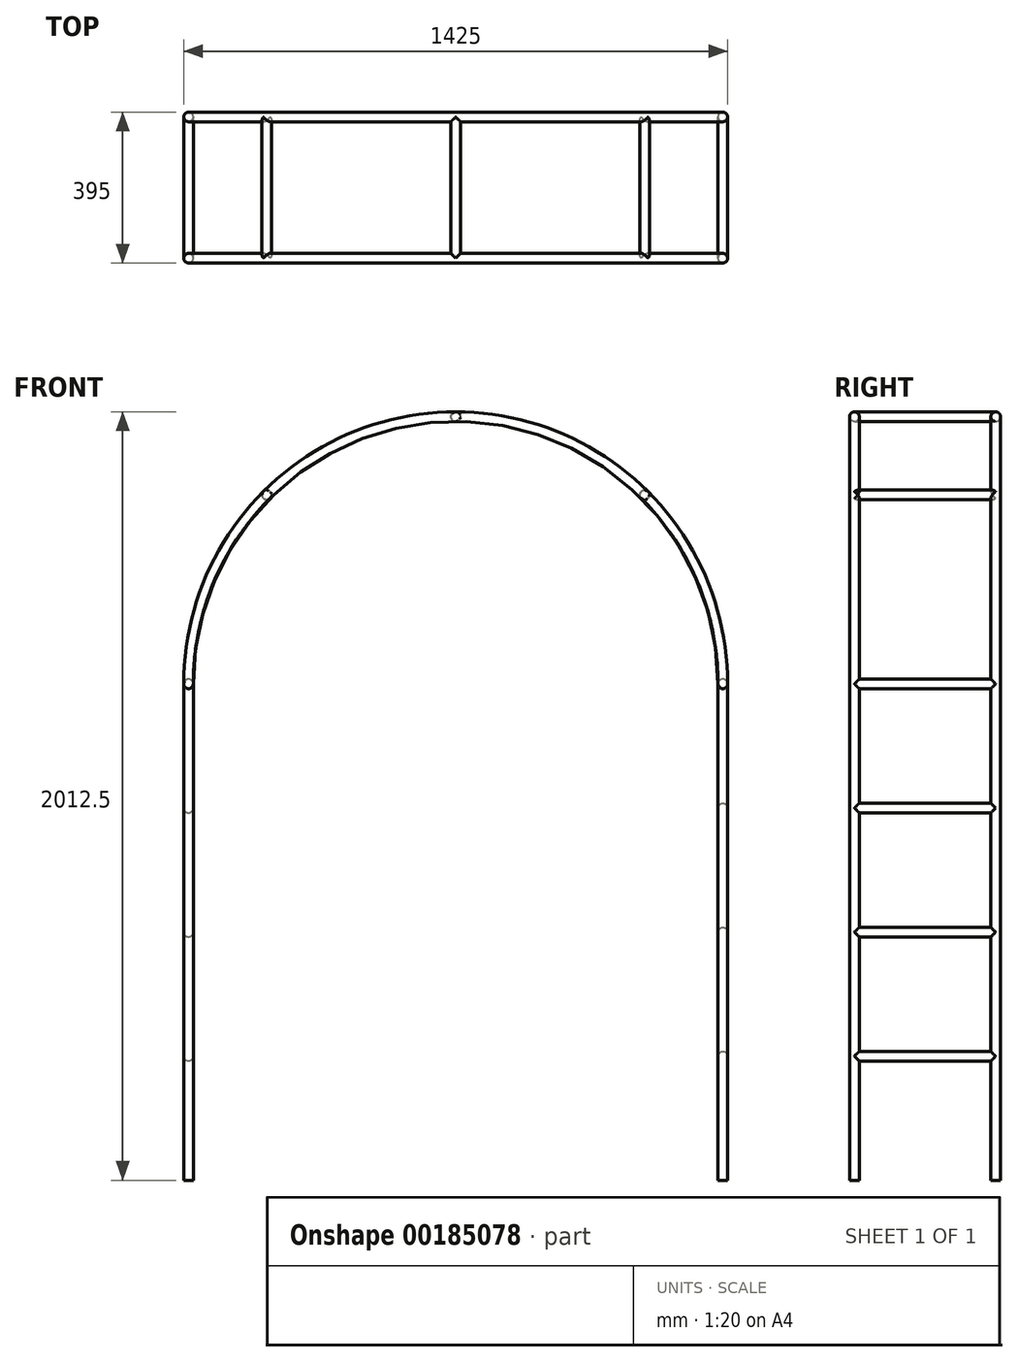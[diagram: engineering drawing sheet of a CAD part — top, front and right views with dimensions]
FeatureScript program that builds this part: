
annotation { "Feature Type Name" : "Feature", "Feature Type Description" : "" }
export const myFeature = defineFeature(function(context is Context, id is Id, definition is map)
    precondition{}
    {
        {
            var Q0;
            Q0=qCreatedBy(makeId("Top.planeOp"),FACE);
            var sketch = newSketch(context, id + "F0", { "sketchPlane" : qUnion([Q0])});
            skCircle(sketch, "E0", {"center": v(-700, 0) * mm, "radius": 12.5 * mm});
            skLineSegment(sketch, "E1", {"start": v(0, 35.36) * mm, "end": v(0, -370) * mm, "construction": true});
            skCircle(sketch, "E2", {"center": v(-700, -370) * mm, "radius": 12.5 * mm});
            skSolve(sketch);
        }
        {
            var Q0;
            Q0=makeQuery(id+"F0.imprint","IMPRINT",FACE,{"disambiguationData":[TD([[makeQuery(id+"F0.imprint","IMPRINT",EDGE,{"derivedFrom":sQuery(id+"F0.wireOp",EDGE,"E0")}),1.0]])]});
            var Q1;
            Q1=makeQuery(id+"F0.imprint","IMPRINT",FACE,{"disambiguationData":[TD([[makeQuery(id+"F0.imprint","IMPRINT",EDGE,{"derivedFrom":sQuery(id+"F0.wireOp",EDGE,"E2")}),1.0]])]});
            var Q2;
            Q2=sQuery(id+"F0.wireOp",EDGE,"E1");
            revolve(context, id + "F1", {"entities" : qUnion([Q0, Q1]), "axis" : qUnion([Q2]), "revolveType" : RevolveType.ONE_DIRECTION, "oppositeDirection" : true, "angle" : 180 * degree});
        }
        {
            var Q0;
            Q0=makeQuery(id+"F1.opRevolve","CAP_FACE",FACE,{"disambiguationData":[OSD([sQuery(id+"F0.wireOp",EDGE,"E0")])],"isStart":true});
            var Q1;
            Q1=makeQuery(id+"F1.opRevolve","CAP_FACE",FACE,{"disambiguationData":[OSD([sQuery(id+"F0.wireOp",EDGE,"E0")])],"isStart":false});
            extrude(context, id + "F2", {"entities" : qUnion([Q0, Q1]), "operationType" : NewBodyOperationType.ADD, "depth" : 1300 * mm});
        }
        {
            var Q0;
            Q0=makeQuery(id+"F1.opRevolve","CAP_FACE",FACE,{"disambiguationData":[OSD([sQuery(id+"F0.wireOp",EDGE,"E2")])],"isStart":true});
            var Q1;
            Q1=makeQuery(id+"F1.opRevolve","CAP_FACE",FACE,{"disambiguationData":[OSD([sQuery(id+"F0.wireOp",EDGE,"E2")])],"isStart":false});
            extrude(context, id + "F3", {"entities" : qUnion([Q0, Q1]), "operationType" : NewBodyOperationType.ADD, "depth" : 1300 * mm});
        }
        {
            var Q0;
            Q0=qCreatedBy(makeId("Front.planeOp"),FACE);
            var sketch = newSketch(context, id + "F4", { "sketchPlane" : qUnion([Q0])});
            skCircle(sketch, "E3", {"center": v(700, -975) * mm, "radius": 12.5 * mm});
            skCircle(sketch, "E4", {"center": v(700, -650) * mm, "radius": 12.5 * mm});
            skCircle(sketch, "E5", {"center": v(700, -325) * mm, "radius": 12.5 * mm});
            skCircle(sketch, "E6", {"center": v(700, 0) * mm, "radius": 12.5 * mm});
            skLineSegment(sketch, "E7", {"start": v(0, 0) * mm, "end": v(0, -1386.76) * mm, "construction": true});
            skCircle(sketch, "E8.MirrorC", {"center": v(-700, 0) * mm, "radius": 12.5 * mm});
            skCircle(sketch, "E9.MirrorC", {"center": v(-700, -325) * mm, "radius": 12.5 * mm});
            skCircle(sketch, "E10.MirrorC", {"center": v(-700, -650) * mm, "radius": 12.5 * mm});
            skCircle(sketch, "E11.MirrorC", {"center": v(-700, -975) * mm, "radius": 12.5 * mm});
            skPoint(sketch, "E12", {"position": v(0, 687.5) * mm});
            skPoint(sketch, "E13", {"position": v(0, 712.5) * mm});
            skLineSegment(sketch, "E14", {"start": v(0, 712.5) * mm, "end": v(0, 687.5) * mm, "construction": true});
            skPoint(sketch, "E15", {"position": v(0, 700) * mm});
            skCircle(sketch, "E16", {"center": v(0, 700) * mm, "radius": 12.5 * mm});
            skPoint(sketch, "E17.start.orphan", {"position": v(687.5, -1300) * mm});
            skCircle(sketch, "E18.1.0", {"center": v(494.97, 494.97) * mm, "radius": 12.5 * mm});
            skPoint(sketch, "E18.center", {"position": v(0, 0) * mm});
            skLineSegment(sketch, "E18.anchor1", {"start": v(0, 0) * mm, "end": v(0, 700) * mm, "construction": true});
            skLineSegment(sketch, "E18.anchor2", {"start": v(0, 0) * mm, "end": v(494.97, 494.97) * mm, "construction": true});
            skCircle(sketch, "E19.MirrorC", {"center": v(-494.97, 494.97) * mm, "radius": 12.5 * mm});
            skSolve(sketch);
        }
        {
            var Q0;
            Q0 = qSketchRegion(id + "F4", true);
            var Q1;
            Q1=sQuery(id+"F0.wireOp",VERTEX,"E2.center");
            extrude(context, id + "F5", {"entities" : qUnion([Q0]), "operationType" : NewBodyOperationType.ADD, "endBound" : BoundingType.UP_TO_VERTEX, "endBoundEntityVertex" : qUnion([Q1]), "depth" : 300 * mm});
        }
    });
